# Revit family: Recycling-Waste-Bins_Aristata-Triple-Full-Full-Full_Busch-Systems
name_source: partatom
category: Specialty Equipment
units: mm (PartAtom-declared; Revit-internal decimal feet)

## family parameters
Always vertical = Yes
Cut with Voids When Loaded = No
Enable Cutting in Views = No
Maintain Annotation Orientation = No
Part Type = Normal
Room Calculation Point = No
Round Connector Dimension = Use Diameter
Shared = No
Work Plane-Based = Yes

## types (5) — shared parameters
Dimension (H x W x D) = 30”H x 39.9375”W x 15”D
Keynote = 11 82 00
Manufacturer = Busch Systems International Inc.
Model = Aristata
Product Page URL = https://www.arcat.com
Sign Frames = Yes
URL = https://www.buschsystems.com
Wheel Casters = Yes
zero-valued in all types: Default Elevation

## type names (no varying parameters)
- Triple Full Full Full-Slate
- Triple Full Full Full-Glacier
- Triple Full Full Full-Mid-Summer Flame
- Triple Full Full Full-Western Breeze
- Triple Full Full Full-Harvest Leaves

note: column(s) folded — value = type name in every type: Product Name

## geometry (parser evidence)
native form markers: Sweep x5
no freeform markers — native parametric forms only
